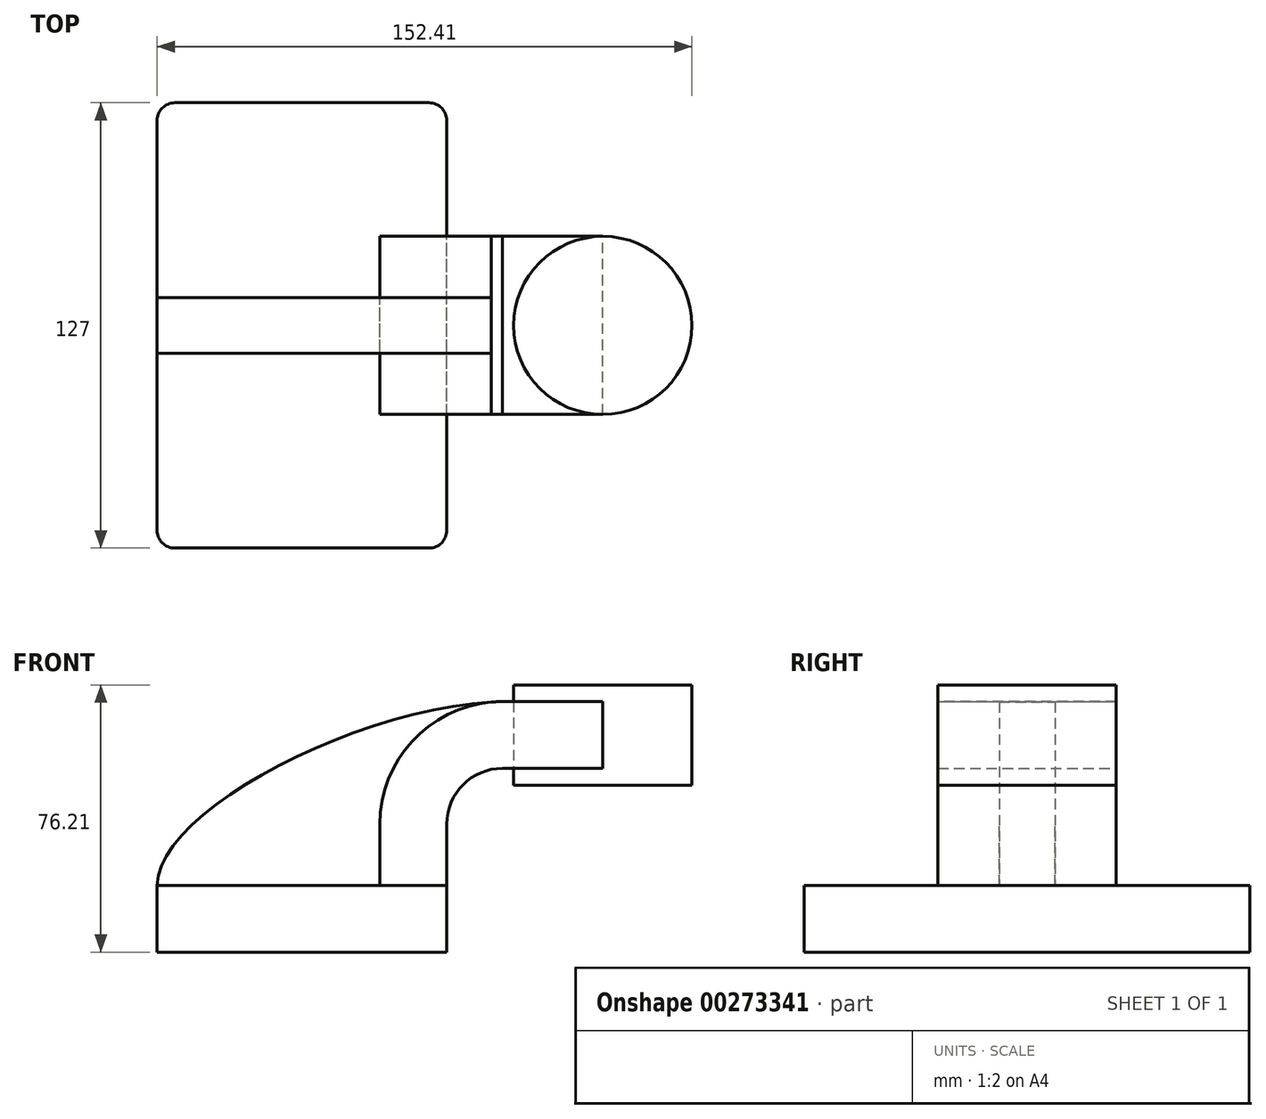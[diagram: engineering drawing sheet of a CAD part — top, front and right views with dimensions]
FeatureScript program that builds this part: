
annotation { "Feature Type Name" : "Feature", "Feature Type Description" : "" }
export const myFeature = defineFeature(function(context is Context, id is Id, definition is map)
    precondition{}
    {
        {
            var Q0;
            Q0=qCreatedBy(makeId("Front.planeOp"),FACE);
            var sketch = newSketch(context, id + "F0", { "sketchPlane" : qUnion([Q0])});
            skLineSegment(sketch, "E0.bottom", {"start": v(-41.28, 9.52) * mm, "end": v(41.27, 9.53) * mm});
            skLineSegment(sketch, "E0.top", {"start": v(-41.28, -9.53) * mm, "end": v(41.28, -9.53) * mm});
            skLineSegment(sketch, "E0.left", {"start": v(-41.28, 9.52) * mm, "end": v(-41.27, -9.53) * mm});
            skLineSegment(sketch, "E0.right", {"start": v(41.28, 9.53) * mm, "end": v(41.28, -9.52) * mm});
            skPoint(sketch, "E0.middle", {"position": v(0, 0) * mm});
            skLineSegment(sketch, "E1.bottom", {"start": v(111.12, 66.67) * mm, "end": v(60.32, 66.67) * mm});
            skLineSegment(sketch, "E1.top", {"start": v(111.12, 38.1) * mm, "end": v(60.33, 38.1) * mm});
            skLineSegment(sketch, "E1.left", {"start": v(111.12, 66.68) * mm, "end": v(111.12, 38.1) * mm});
            skLineSegment(sketch, "E1.right", {"start": v(60.32, 66.68) * mm, "end": v(60.33, 38.1) * mm});
            skPoint(sketch, "E1.middle", {"position": v(85.72, 52.39) * mm});
            skLineSegment(sketch, "E2", {"start": v(41.27, 9.53) * mm, "end": v(41.27, 27) * mm});
            skArc(sketch, "E3", {"start": v(41.27, 27) * mm, "mid": v(45.92, 38.23) * mm, "end": v(57.15, 42.88) * mm});
            skLineSegment(sketch, "E4", {"start": v(57.15, 42.88) * mm, "end": v(85.72, 42.88) * mm});
            skLineSegment(sketch, "E5.0", {"start": v(57.15, 61.93) * mm, "end": v(85.72, 61.93) * mm});
            skArc(sketch, "E5.1", {"start": v(22.22, 27) * mm, "mid": v(32.45, 51.7) * mm, "end": v(57.15, 61.93) * mm});
            skLineSegment(sketch, "E5.2", {"start": v(22.22, 9.53) * mm, "end": v(22.22, 27) * mm});
            skLineSegment(sketch, "E6", {"start": v(85.72, 61.93) * mm, "end": v(85.72, 42.88) * mm});
            skLineSegment(sketch, "E7", {"start": v(22.22, 9.53) * mm, "end": v(41.27, 9.53) * mm});
            skLineSegment(sketch, "E8", {"start": v(85.72, 38.1) * mm, "end": v(85.72, 66.67) * mm});
            skFitSpline(sketch, "E9", {"points": [v(57.15, 61.93) * mm, v(-41.28, 9.52) * mm], "startDerivative": vector(-124.34, -3.51) * mm, "endDerivative": vector(0, -62.84) * mm});
            skSolve(sketch);
        }
        {
            var Q0;
            Q0=makeQuery(id+"F0.imprint","IMPRINT",FACE,{"disambiguationData":[TD([[makeQuery(id+"F0.imprint","IMPRINT",EDGE,{"derivedFrom":sQuery(id+"F0.wireOp",EDGE,"E0.bottom")}),-1.0]])]});
            extrude(context, id + "F1", {"entities" : qUnion([Q0]), "endBound" : BoundingType.SYMMETRIC, "depth" : 127 * mm});
        }
        {
            var Q0;
            Q0=makeQuery(id+"F0.imprint","IMPRINT",FACE,{"disambiguationData":[TD([[makeQuery(id+"F0.imprint","IMPRINT",EDGE,{"derivedFrom":sQuery(id+"F0.wireOp",EDGE,"E2")}),1.0]])]});
            var Q1;
            {var subQ0=sQuery(id+"F0.wireOp",EDGE,"E5.0");var subQ1=sQuery(id+"F0.wireOp",EDGE,"E1.right");var subQ2=makeQuery(id+"F0.imprint","INTERSECT",VERTEX,{"derivedFrom":[subQ1,subQ0]});Q1=makeQuery(id+"F0.imprint","IMPRINT",FACE,{"disambiguationData":[TD([[makeQuery(id+"F0.imprint","IMPRINT",EDGE,{"disambiguationData":[TD([[subQ2,-1.0]])],"derivedFrom":subQ1}),1.0]])]});}
            extrude(context, id + "F2", {"entities" : qUnion([Q0, Q1]), "endBound" : BoundingType.SYMMETRIC, "depth" : 50.8 * mm});
        }
        {
            var Q0;
            {var subQ0=sQuery(id+"F0.wireOp",EDGE,"E0.bottom");Q0=makeQuery(id+"F0.imprint","IMPRINT",FACE,{"disambiguationData":[TD([[makeQuery(id+"F0.imprint","IMPRINT",EDGE,{"derivedFrom":subQ0}),1.0]])]});}
            extrude(context, id + "F3", {"entities" : qUnion([Q0]), "endBound" : BoundingType.SYMMETRIC, "depth" : 15.88 * mm});
        }
        {
            var Q0;
            {var subQ0=sQuery(id+"F0.wireOp",EDGE,"E1.left");Q0=makeQuery(id+"F0.imprint","IMPRINT",FACE,{"disambiguationData":[TD([[makeQuery(id+"F0.imprint","IMPRINT",EDGE,{"derivedFrom":subQ0}),-1.0]])]});}
            var Q1;
            Q1=sQuery(id+"F0.wireOp",EDGE,"E8");
            revolve(context, id + "F4", {"entities" : qUnion([Q0]), "axis" : qUnion([Q1]), "revolveType" : RevolveType.FULL});
        }
        {
            var Q0;
            Q0=makeQuery(id+"F1.opExtrude","CAP_EDGE",EDGE,{"disambiguationData":[OSD([sQuery(id+"F0.wireOp",EDGE,"E0.right")])],"isStart":false});
            var Q1;
            Q1=makeQuery(id+"F1.opExtrude","CAP_EDGE",EDGE,{"disambiguationData":[OSD([sQuery(id+"F0.wireOp",EDGE,"E0.left")])],"isStart":false});
            var Q2;
            Q2=makeQuery(id+"F1.opExtrude","CAP_EDGE",EDGE,{"disambiguationData":[OSD([sQuery(id+"F0.wireOp",EDGE,"E0.right")])],"isStart":true});
            var Q3;
            Q3=makeQuery(id+"F1.opExtrude","CAP_EDGE",EDGE,{"disambiguationData":[OSD([sQuery(id+"F0.wireOp",EDGE,"E0.left")])],"isStart":true});
            fillet(context, id + "F5", {"entities" : qUnion([Q0, Q1, Q2, Q3]), "radius" : 5.08 * mm, "tangentPropagation" : true, "allowEdgeOverflow" : false});
        }
    });
